# Revit family: Chaine de traitement par Absorption (support au sol) - AD 5035 et AD 5065
name_source: partatom
category: Equipement spécialisé
revit_build: Autodesk Revit 2018 (Build: 20170223_1515(x64)
units: mm (PartAtom-declared; Revit-internal decimal feet)

## family parameters
Basée sur le plan de construction = Non
Cote de connecteur circulaire = Utiliser le diamètre
Couper avec des vides une fois chargée = Non
Partagée = Non
Point de calcul de pièce = Non
Toujours verticalement = Oui
Type d'élément = Normal

## types (2) — shared parameters
COS_PHI = 0.9
DESCR_ALIM_X = Alimentation X ; 3G1 mm²
DIAM_SORTIE_AIR = 20 mm  [stored 0.0656168 ft]
Diametre_Percement_1 = 11 mm  [stored 0.0360892 ft]
Diametre_Percement_2 = 14 mm  [stored 0.0459318 ft]
Diametre_Percement_3 = 25 mm  [stored 0.082021 ft]
Entraxe_Horizontal_Percement_1 = 410 mm  [stored 1.34514 ft]
Entraxe_Horizontal_Percement_2 = 410 mm  [stored 1.34514 ft]
Entraxe_Rouleau = 313 mm  [stored 1.0269 ft]
Entraxe_Vertical_Percement_2 = 150 mm
FREQUENCE = 50 Hz
Fabricant = MIL'S
Hauteur_Boitier_Commande = 1050 mm
Hauteur_Filtres = 800 mm  [stored 2.62467 ft]
LARGEUR = 460 mm  [stored 1.50919 ft]
LONGUEUR = 250 mm  [stored 0.82021 ft]
Largeur_Support = 460 mm  [stored 1.50919 ft]
Lien espace client = https://www.mils.fr
NBR_POLES = 1
NEUTRE = Oui
PROTEC_ELECT_X = Disjoncteur coube D - 1 A
PUISS_APPARENTE_X = 167 VA
PUISS_ELECT_X = 0 kW
Profondeur_Support = 250 mm  [stored 0.82021 ft]
TENSION_ALIM = 230 V
TERRE = Oui

## per-type parameters (varying)
| type | DEBIT_ENTREE_AIR | DEBIT_SORTIE_AIR | DESCR_ENTREE_AIR | DESCR_SORTIE_AIR | DIAM_ENTREE_AIR | Entraxe_Vertical_Percement_1 | HAUTEUR | Hauteur_Detente | Hauteur_Rouleau | Hauteur_Support | Hauteur_Vidange | Longueur_Rouleau | Modèle | POIDS(Kg) |
| SEC 7 HC - AD 5035 | 35.0 m³/h | 35.0 m³/h | Entrée Air ; 35 m3/h à 10 bar ; ID G 3/8" | Sortie Air ; 35 m3/h à 10 bar ; ID G 3/4" ; | 12 mm  [stored 0.0393701 ft] | 300 mm | 1305 mm  [stored 4.2815 ft] | 1200 mm  [stored 3.93701 ft] | 283 mm | 1305 mm  [stored 4.2815 ft] | 300 mm | 950 mm  [stored 3.1168 ft] | SEC HC - AD 5035 | 50 mm  [stored 0.164042 ft] |
| SEC 7 HC - AD 5065 | 65.0 m³/h | 65.0 m³/h | Entrée Air ; 65 m3/h à 10 bar ; ID G 1/2" | Sortie Air ; 65 m3/h à 10 bar ; ID G 3/4" ; | 15 mm  [stored 0.0492126 ft] | 400 mm  [stored 1.31234 ft] | 1570 mm | 1490 mm  [stored 4.88845 ft] | 25 mm  [stored 0.082021 ft] | 1570 mm | 50 mm  [stored 0.164042 ft] | 1500 mm  [stored 4.92126 ft] | SEC HC - AD 5065 | 60 mm  [stored 0.19685 ft] |

note: [stored X ft] marks values corroborated as IEEE doubles in the binary element streams (Revit-internal decimal feet)
